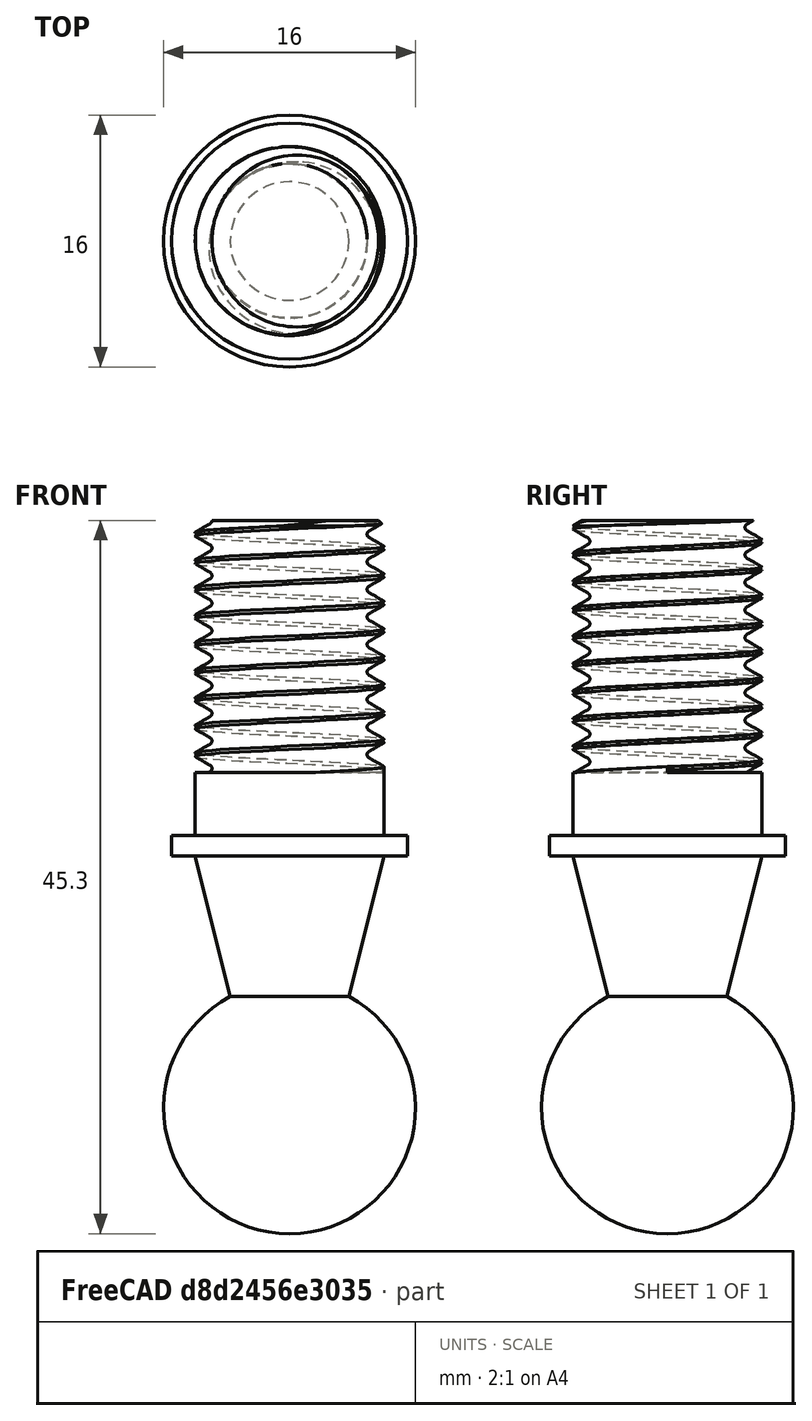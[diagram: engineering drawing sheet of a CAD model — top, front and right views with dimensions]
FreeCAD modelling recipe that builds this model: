
FCSTD DOCUMENT  (FreeCAD 1.0R39109 (Git))
Label: 7
License: All rights reserved
LicenseURL: https://en.wikipedia.org/wiki/All_rights_reserved
objects: Part::Cylinder×2, Part::Cone×1, Part::Sphere×1, Part::FeaturePython×1, Part::Chamfer×1, Part::Cut×1, Part::MultiFuse×1
note: 8 computed .brp shape members not serialized (recipe doc carries the construction recipe); baked Part::Feature solids carry a one-line shape summary decoded from their .brp

FEATURE [Part::Cone] Cone  label="Конус"
  Angle = 360
  AttacherType = Attacher::AttachEngine3D
  Height = 24
  Radius1 = 0
  Radius2 = 6
FEATURE [Part::Sphere] Sphere  label="Сфера"
  Angle1 = -90
  Angle2 = 90
  Angle3 = 360
  AttacherType = Attacher::AttachEngine3D
  Placement = pos=(0,0,8) rot=(0,0,1;0rad)
  Radius = 8
FEATURE [Part::Cylinder] Cylinder  label="Цилиндр"
  Angle = 360
  AttacherType = Attacher::AttachEngine3D
  FirstAngle = 0
  Height = 1.3
  Placement = pos=(0,0,24) rot=(0,0,1;0rad)
  Radius = 7.5
  SecondAngle = 0
FEATURE [Part::Cylinder] Cylinder001  label="Цилиндр001"
  Angle = 360
  AttacherType = Attacher::AttachEngine3D
  FirstAngle = 0
  Height = 20
  Placement = pos=(0,0,25.3) rot=(0,0,1;0rad)
  Radius = 6
  SecondAngle = 0
FEATURE [Part::FeaturePython] ScrewDie  label="M12x16-Плашка"  # WARN: FeaturePython — macro-defined, semantics opaque (R4)
  Diameter = 11
  DiameterCustom = 6
  Invert = false
  LeftHanded = false
  Length = 16
  MatchOuter = false
  OffsetAngle = 0
  PitchCustom = 1
  Placement = pos=(0,0,45.3) rot=(0,0,1;0rad)
  Thread = true
  Type = 0
FEATURE [Part::Chamfer] Chamfer
  Base = -> Cylinder001
  EdgeLinks = -> Cylinder001 [Edge3]
  Edges = 1 edges r=0.35: [Edge3]
FEATURE [Part::Cut] Cut
  Base = -> Chamfer
  Refine = true
  Tool = -> ScrewDie
FEATURE [Part::MultiFuse] Fusion
  Refine = true
  Shapes = -> [Sphere,Cylinder,Cut,Cone]
